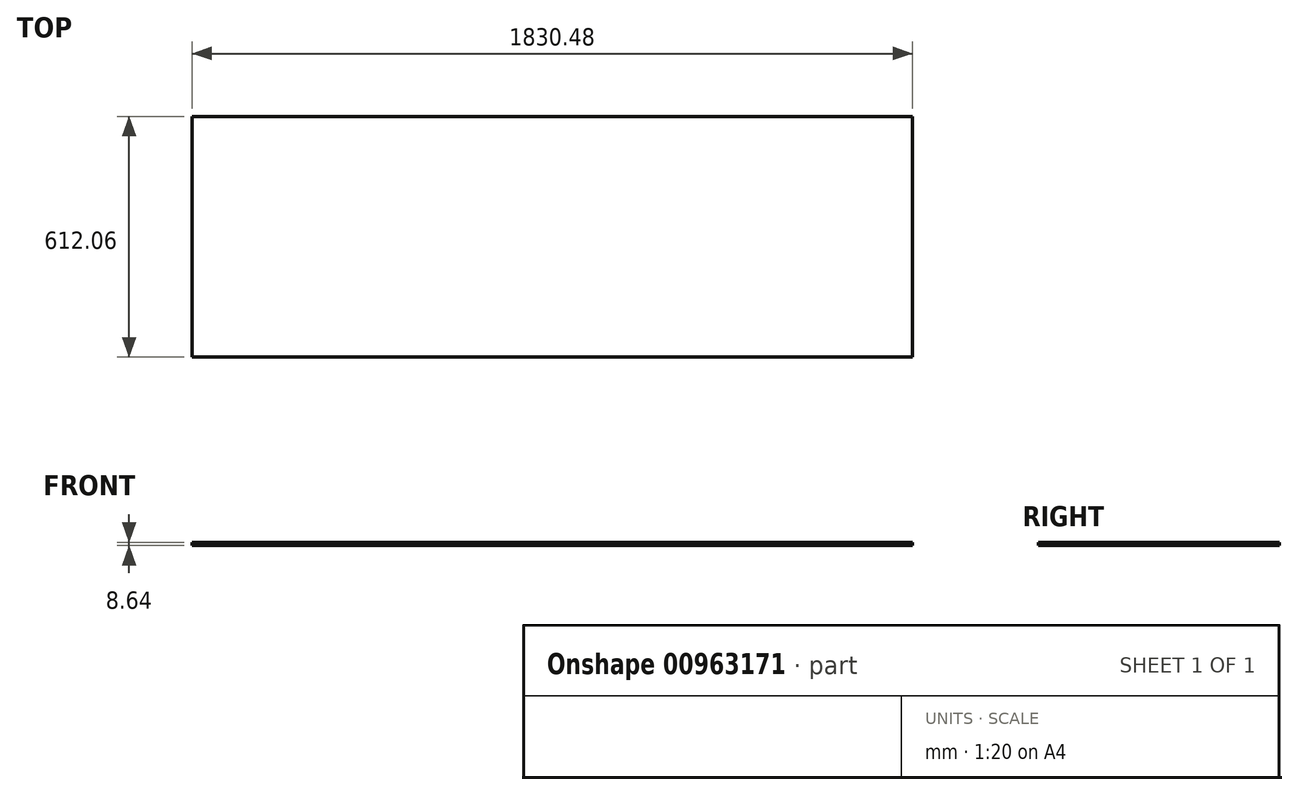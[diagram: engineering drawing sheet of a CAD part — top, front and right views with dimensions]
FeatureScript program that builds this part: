
annotation { "Feature Type Name" : "Feature", "Feature Type Description" : "" }
export const myFeature = defineFeature(function(context is Context, id is Id, definition is map)
    precondition{}
    {
        {
            var Q0;
            Q0=qCreatedBy(makeId("Top.planeOp"),FACE);
            var sketch = newSketch(context, id + "F0", { "sketchPlane" : qUnion([Q0])});
            skLineSegment(sketch, "E0.bottom", {"start": v(-915.24, 306.03) * mm, "end": v(915.24, 306.03) * mm});
            skLineSegment(sketch, "E0.top", {"start": v(-915.24, -306.03) * mm, "end": v(915.24, -306.03) * mm});
            skLineSegment(sketch, "E0.left", {"start": v(-915.24, 306.03) * mm, "end": v(-915.24, -306.03) * mm});
            skLineSegment(sketch, "E0.right", {"start": v(915.24, 306.03) * mm, "end": v(915.24, -306.03) * mm});
            skPoint(sketch, "E0.middle", {"position": v(0, 0) * mm});
            skSolve(sketch);
        }
        {
            var Q0;
            Q0=makeQuery(id+"F0.imprint","IMPRINT",FACE,{"disambiguationData":[TD([[makeQuery(id+"F0.imprint","IMPRINT",EDGE,{"derivedFrom":sQuery(id+"F0.wireOp",EDGE,"E0.bottom")}),-1.0]])]});
            extrude(context, id + "F1", {"entities" : qUnion([Q0]), "depth" : 8.64 * mm, "offsetDistance" : 25.4 * mm});
        }
    });
